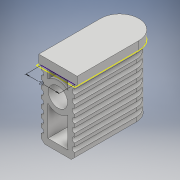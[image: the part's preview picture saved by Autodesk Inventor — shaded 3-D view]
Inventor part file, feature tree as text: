
AUTODESK INVENTOR PART (.ipt)
format: ipt  version: 2018 (Build 220112000, 112)  size: 244,736 bytes
history: native  units: mm
features: extrude x5, sketch x5, projected_geometry x3, chamfer x2, mirror x1
ambient origin geometry x8: Origin, YZ Plane, XZ Plane, XY Plane, X Axis, Y Axis, Z Axis, Center Point
bodies: Solid1 (feature_tree)
feature tree (16):
  extrude  "Extrusion1"  Depth=11.5mm
  extrude  "Extrusion2"  Depth=20.0mm
  extrude  "Extrusion3"  Depth=11.5mm
  extrude  "Extrusion4"  Depth=11.5mm
  mirror  "Mirror1"
  chamfer  "Chamfer1"  Distance=40.0mm
  chamfer  "Chamfer2"  Distance=5.0mm
  extrude  "Extrusion5"  Depth=5.0mm
  sketch  "Sketch1"  dims[d0=38.5mm d1=11.5mm]
  sketch  "Sketch2"  dims[d2=5.0mm d3=0.0mm d4=20.0mm]
  projected_geometry  "Projected Loop1"
  sketch  "Sketch3"  dims[d5=40.0mm d6=0.0mm d8=11.5mm]
  projected_geometry  "Projected Loop2"
  sketch  "Sketch4"  dims[d9=3.0mm d10=11.5mm d11=40.0mm d12=0.0mm]
  projected_geometry  "Projected Loop3"
  sketch  "Sketch5"  dims[d13=17.0mm d14=5.0mm d15=5.0mm d16=5.0mm d17=5.0mm d18=5.0mm d19=5.0mm d20=40.0mm d21=0.0mm d22=2.0mm d23=2.0mm d24=45.0deg d25=4.0mm d26=2.0mm d27=45.0deg d28=40.0mm d29=0.0mm d31=4.0mm d32=4.0mm d33=4.0mm]
